# Revit family: ElectricalEquipment_Hager_DINRailEnclosures
name_source: partatom
category: Electrical Equipment
revit_build: Autodesk Revit 2015 (Build: 20160512_1515(x64)
units: mm (PartAtom-declared; Revit-internal decimal feet)

## types (8) — shared parameters
Assembly Code = D5010
AssetType = Fixed
Category = ElectricalEquipment
ClassificationName = Uniclass2015
ClassificationValue = Pr_80_77_28_16
Colour = RAL 9010 White Gloss
Default Elevation = 500 mm  [stored 1.64042 ft]
DocumentationLiterature = http://www.hager.co.uk
DocumentationTechnical = http://www.hager.co.uk
DurationUnit = Years
ExpectedLife = 10
IfcExportAs = ElectricalEquipment
Keynote = V
Mains Type = AC
Manufacturer = Hager
ManufacturerName = Hager
Material = MildSteel,ABS,AcousticComposite
NBSDescription = ElectricalEquipment
NBSReference = Pr_80_77_28_16
Neutral Rating = 100.00%
NominalHeight = 125 mm  [stored 0.410105 ft]
Shape = Rectangular
TypeName = ElectricalEquipment
URL = http://www.hager.co.uk
WarrantyDescription = See Manufacturer
WarrantyDurationParts = 2
WarrantyDurationUnit = Years
WarrantyGuarantorParts = 2
_BimstoreBibleVersion = V14
_DistributedBy = www.bimstore.co.uk
zero-valued in all types: NominalDepth, ReplacementCost, ServiceLifeDuration, WarrantyDurationLabor, _BimSpecGuid, _CurrentRevision

## per-type parameters (varying)
| type | BIMObjectName | Description | EAN | Features | NBSObjectName | NominalLength | NominalWidth | Voltage |
| JK008 | Hager_ElectricalEquipment_DINRailEnclosures_JK008 | 8Mod_DINRailBoxPlain | 3250610433324 | 8Mod_DINRailBoxPlain | Hager_DINRailEnclosures_JK008 | 254 mm | 236 mm |  |
| JK012 | Hager_ElectricalEquipment_DINRailEnclosures_JK012 | 12Mod_DINRailBoxPlain | 3250610433348 | 12Mod_DINRailBoxPlain | Hager_DINRailEnclosures_JK012 | 236 mm | 326 mm  [stored 1.06955 ft] |  |
| JK016 | Hager_ElectricalEquipment_DINRailEnclosures_JK016 | 16Mod_DINRailBoxPlain | 3250610433362 | 16Mod_DINRailBoxPlain | Hager_DINRailEnclosures_JK016 | 236 mm | 397 mm  [stored 1.30249 ft] |  |
| JK022 | Hager_ElectricalEquipment_DINRailEnclosures_JK022 | 22Mod_DINRailBoxPlain | 3250610433386 | 22Mod_DINRailBoxPlain | Hager_DINRailEnclosures_JK022 | 236 mm | 505 mm  [stored 1.65682 ft] |  |
| JK024 | Hager_ElectricalEquipment_DINRailEnclosures_JK024 | 24Mod_DINRailBoxPlain | 3250610433409 | 24Mod_DINRailBoxPlain | Hager_DINRailEnclosures_JK024 | 236 mm | 505 mm  [stored 1.65682 ft] |  |
| JK032 | Hager_ElectricalEquipment_DINRailEnclosures_JK032 | 32Mod_DINRailBoxPlain | 3250610433423 | 32Mod_DINRailBoxPlain | Hager_DINRailEnclosures_JK032 | 472 mm | 397 mm  [stored 1.30249 ft] |  |
| JK044 | Hager_ElectricalEquipment_DINRailEnclosures_JK044 | 44Mod_DINRailBoxPlain | 3250610433447 | 44Mod_DINRailBoxPlain | Hager_DINRailEnclosures_JK044 | 472 mm | 397 mm  [stored 1.30249 ft] |  |
| JK066 | Hager_ElectricalEquipment_DINRailEnclosures_JK066 | 66Mod_DINRailBoxPlain | 3250610433461 | 66Mod_DINRailBoxPlain | Hager_DINRailEnclosures_JK066 | 708 mm  [stored 2.32283 ft] | 397 mm  [stored 1.30249 ft] | 230V |

note: column(s) folded — value = type name in every type: Model, Type Comments

note: [stored X ft] marks values corroborated as IEEE doubles in the binary element streams (Revit-internal decimal feet)

## geometry (parser evidence)
native form markers: Blend x2, Sweep x3
no freeform markers — native parametric forms only
